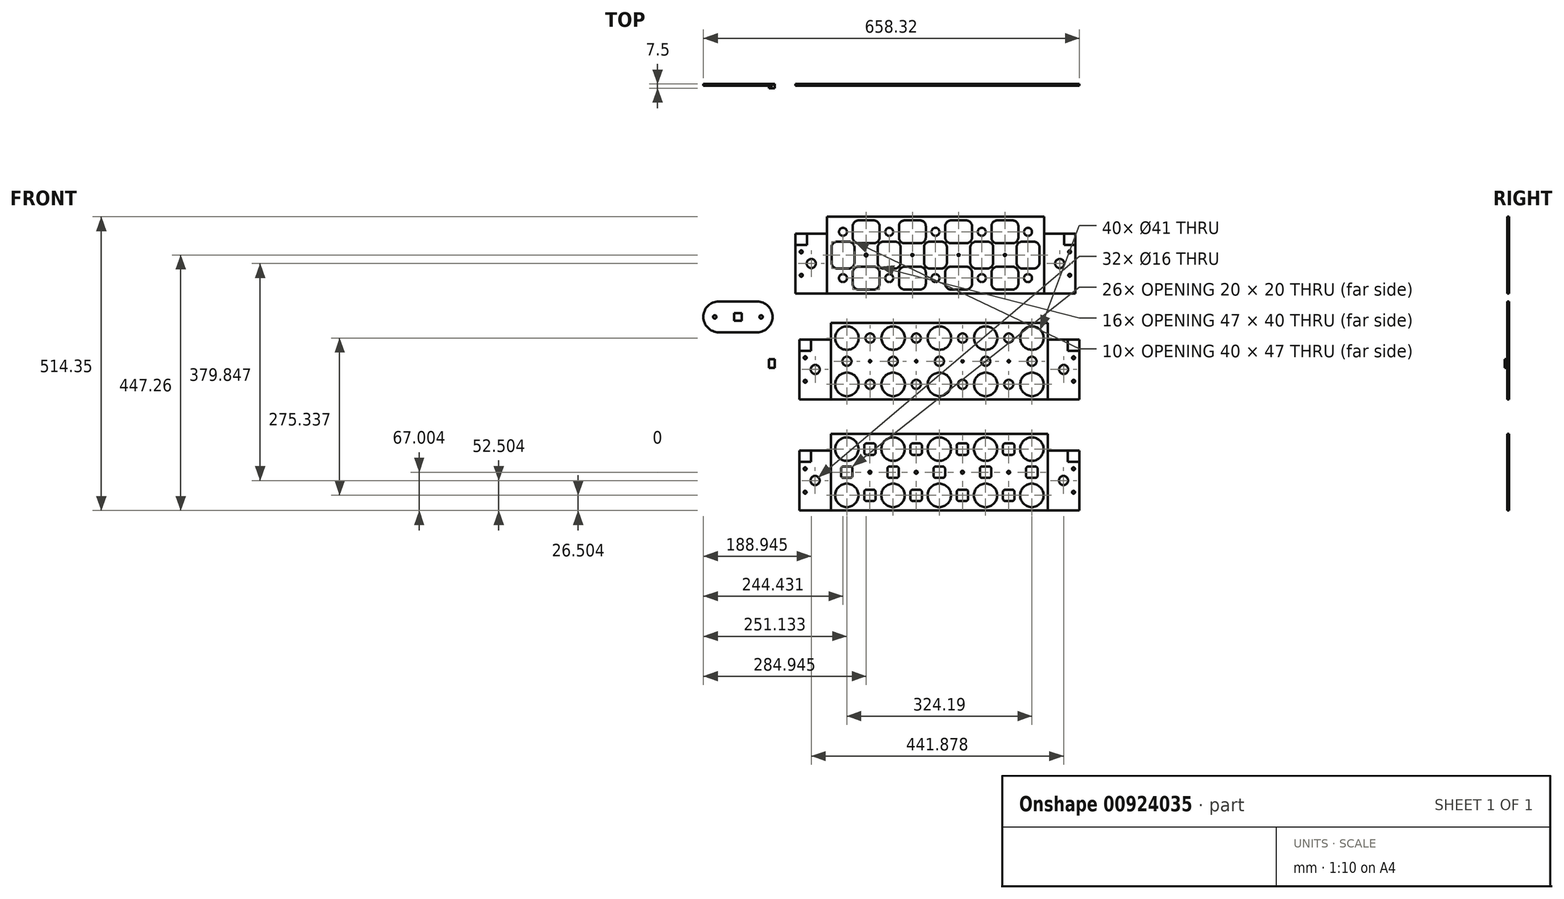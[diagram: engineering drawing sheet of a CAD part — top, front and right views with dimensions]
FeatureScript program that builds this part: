
annotation { "Feature Type Name" : "Feature", "Feature Type Description" : "" }
export const myFeature = defineFeature(function(context is Context, id is Id, definition is map)
    precondition{}
    {
        {
            var Q0;
            Q0=qCreatedBy(makeId("Front.planeOp"),FACE);
            var sketch = newSketch(context, id + "F0", { "sketchPlane" : qUnion([Q0])});
            skLineSegment(sketch, "E0.bottom", {"start": v(-471.38, 281.14) * mm, "end": v(-91.38, 281.14) * mm});
            skLineSegment(sketch, "E0.top", {"start": v(-471.38, 146.64) * mm, "end": v(-91.38, 146.64) * mm});
            skLineSegment(sketch, "E0.left", {"start": v(-471.38, 281.14) * mm, "end": v(-471.38, 146.64) * mm});
            skLineSegment(sketch, "E0.right", {"start": v(-91.38, 281.14) * mm, "end": v(-91.38, 146.64) * mm});
            skLineSegment(sketch, "E1.bottom", {"start": v(-471.38, 251.64) * mm, "end": v(-526.38, 251.64) * mm});
            skLineSegment(sketch, "E1.top", {"start": v(-471.38, 146.64) * mm, "end": v(-526.38, 146.64) * mm});
            skLineSegment(sketch, "E1.left", {"start": v(-471.38, 251.64) * mm, "end": v(-471.38, 146.64) * mm});
            skLineSegment(sketch, "E1.right", {"start": v(-526.38, 251.64) * mm, "end": v(-526.38, 146.64) * mm});
            skLineSegment(sketch, "E2.bottom", {"start": v(-91.38, 251.64) * mm, "end": v(-36.38, 251.64) * mm});
            skLineSegment(sketch, "E2.top", {"start": v(-91.38, 146.64) * mm, "end": v(-36.38, 146.64) * mm});
            skLineSegment(sketch, "E2.left", {"start": v(-91.38, 251.64) * mm, "end": v(-91.38, 146.64) * mm});
            skLineSegment(sketch, "E2.right", {"start": v(-36.38, 251.64) * mm, "end": v(-36.38, 146.64) * mm});
            skCircle(sketch, "E3", {"center": v(-443.38, 173.64) * mm, "radius": 7 * mm});
            skCircle(sketch, "E4.0.1.0", {"center": v(-443.38, 254.64) * mm, "radius": 7 * mm});
            skCircle(sketch, "E4.1.0.0", {"center": v(-362.38, 173.64) * mm, "radius": 7 * mm});
            skCircle(sketch, "E4.1.1.0", {"center": v(-362.38, 254.64) * mm, "radius": 7 * mm});
            skCircle(sketch, "E4.2.0.0", {"center": v(-281.38, 173.64) * mm, "radius": 7 * mm});
            skCircle(sketch, "E4.2.1.0", {"center": v(-281.38, 254.64) * mm, "radius": 7 * mm});
            skCircle(sketch, "E4.3.0.0", {"center": v(-200.38, 173.64) * mm, "radius": 7 * mm});
            skCircle(sketch, "E4.3.1.0", {"center": v(-200.38, 254.64) * mm, "radius": 7 * mm});
            skCircle(sketch, "E4.4.0.0", {"center": v(-119.38, 173.64) * mm, "radius": 7 * mm});
            skCircle(sketch, "E4.4.1.0", {"center": v(-119.38, 254.64) * mm, "radius": 7 * mm});
            skLineSegment(sketch, "E4.direction1", {"start": v(-443.38, 173.64) * mm, "end": v(-362.38, 173.64) * mm, "construction": true});
            skLineSegment(sketch, "E4.direction2", {"start": v(-443.38, 173.64) * mm, "end": v(-443.38, 254.64) * mm, "construction": true});
            skCircle(sketch, "E5", {"center": v(-498.88, 199.14) * mm, "radius": 8 * mm});
            skCircle(sketch, "E6", {"center": v(-63.88, 199.14) * mm, "radius": 8 * mm});
            skPoint(sketch, "E7", {"position": v(-63.88, 251.64) * mm});
            skPoint(sketch, "E8", {"position": v(-498.88, 251.64) * mm});
            skLineSegment(sketch, "E9.bottom", {"start": v(-526.38, 166.64) * mm, "end": v(-506.38, 166.64) * mm});
            skLineSegment(sketch, "E9.top", {"start": v(-526.38, 146.64) * mm, "end": v(-506.38, 146.64) * mm});
            skLineSegment(sketch, "E9.left", {"start": v(-526.38, 166.64) * mm, "end": v(-526.38, 146.64) * mm});
            skLineSegment(sketch, "E9.right", {"start": v(-506.38, 166.64) * mm, "end": v(-506.38, 146.64) * mm});
            skLineSegment(sketch, "E10.bottom", {"start": v(-526.38, 251.64) * mm, "end": v(-506.38, 251.64) * mm});
            skLineSegment(sketch, "E10.top", {"start": v(-526.38, 231.64) * mm, "end": v(-506.38, 231.64) * mm});
            skLineSegment(sketch, "E10.left", {"start": v(-526.38, 251.64) * mm, "end": v(-526.38, 231.64) * mm});
            skLineSegment(sketch, "E10.right", {"start": v(-506.38, 251.64) * mm, "end": v(-506.38, 231.64) * mm});
            skLineSegment(sketch, "E11.bottom", {"start": v(-36.38, 251.64) * mm, "end": v(-56.38, 251.64) * mm});
            skLineSegment(sketch, "E11.top", {"start": v(-36.38, 231.64) * mm, "end": v(-56.38, 231.64) * mm});
            skLineSegment(sketch, "E11.left", {"start": v(-36.38, 251.64) * mm, "end": v(-36.38, 231.64) * mm});
            skLineSegment(sketch, "E11.right", {"start": v(-56.38, 251.64) * mm, "end": v(-56.38, 231.64) * mm});
            skLineSegment(sketch, "E12.bottom", {"start": v(-36.38, 146.64) * mm, "end": v(-56.38, 146.64) * mm});
            skLineSegment(sketch, "E12.top", {"start": v(-36.38, 166.64) * mm, "end": v(-56.38, 166.64) * mm});
            skLineSegment(sketch, "E12.left", {"start": v(-36.38, 146.64) * mm, "end": v(-36.38, 166.64) * mm});
            skLineSegment(sketch, "E12.right", {"start": v(-56.38, 146.64) * mm, "end": v(-56.38, 166.64) * mm});
            skPoint(sketch, "E13", {"position": v(-506.38, 241.64) * mm});
            skPoint(sketch, "E14", {"position": v(-506.38, 156.64) * mm});
            skPoint(sketch, "E15", {"position": v(-56.38, 241.64) * mm});
            skPoint(sketch, "E16", {"position": v(-56.38, 156.64) * mm});
            skCircle(sketch, "E17", {"center": v(-402.88, 214.14) * mm, "radius": 2.55 * mm});
            skCircle(sketch, "E18.1.0.0", {"center": v(-321.88, 214.14) * mm, "radius": 2 * mm});
            skCircle(sketch, "E18.2.0.0", {"center": v(-240.88, 214.14) * mm, "radius": 2 * mm});
            skCircle(sketch, "E18.3.0.0", {"center": v(-159.88, 214.14) * mm, "radius": 2 * mm});
            skPoint(sketch, "E19", {"position": v(-36.38, 199.14) * mm});
            skPoint(sketch, "E20", {"position": v(-516.38, 231.64) * mm});
            skPoint(sketch, "E21", {"position": v(-516.38, 166.64) * mm});
            skPoint(sketch, "E22", {"position": v(-46.38, 231.64) * mm});
            skPoint(sketch, "E23", {"position": v(-46.38, 166.64) * mm});
            skCircle(sketch, "E24", {"center": v(-516.38, 219.64) * mm, "radius": 2.55 * mm});
            skCircle(sketch, "E25", {"center": v(-516.38, 178.64) * mm, "radius": 2.55 * mm});
            skCircle(sketch, "E26", {"center": v(-46.38, 219.64) * mm, "radius": 2.55 * mm});
            skCircle(sketch, "E27", {"center": v(-46.38, 178.64) * mm, "radius": 2.55 * mm});
            skLineSegment(sketch, "E28.bottom", {"start": v(-464.5, 95.13) * mm, "end": v(-84.5, 95.13) * mm});
            skLineSegment(sketch, "E28.top", {"start": v(-464.5, -38.87) * mm, "end": v(-84.5, -38.87) * mm});
            skLineSegment(sketch, "E28.left", {"start": v(-464.5, 95.13) * mm, "end": v(-464.5, -38.87) * mm});
            skLineSegment(sketch, "E28.right", {"start": v(-84.5, 95.13) * mm, "end": v(-84.5, -38.87) * mm});
            skLineSegment(sketch, "E29.bottom", {"start": v(-464.5, 66.13) * mm, "end": v(-519.5, 66.13) * mm});
            skLineSegment(sketch, "E29.top", {"start": v(-464.5, -38.87) * mm, "end": v(-519.5, -38.87) * mm});
            skLineSegment(sketch, "E29.left", {"start": v(-464.5, 66.13) * mm, "end": v(-464.5, -38.87) * mm});
            skLineSegment(sketch, "E29.right", {"start": v(-519.5, 66.13) * mm, "end": v(-519.5, -38.87) * mm});
            skLineSegment(sketch, "E30.bottom", {"start": v(-84.5, 66.13) * mm, "end": v(-29.5, 66.13) * mm});
            skLineSegment(sketch, "E30.top", {"start": v(-84.5, -38.87) * mm, "end": v(-29.5, -38.87) * mm});
            skLineSegment(sketch, "E30.left", {"start": v(-84.5, 66.13) * mm, "end": v(-84.5, -38.87) * mm});
            skLineSegment(sketch, "E30.right", {"start": v(-29.5, 66.13) * mm, "end": v(-29.5, -38.87) * mm});
            skCircle(sketch, "E31", {"center": v(-436.5, -12.37) * mm, "radius": 20.5 * mm});
            skCircle(sketch, "E32.0.1.0", {"center": v(-436.5, 68.63) * mm, "radius": 20.5 * mm});
            skCircle(sketch, "E32.1.0.0", {"center": v(-355.5, -12.37) * mm, "radius": 20.5 * mm});
            skCircle(sketch, "E32.1.1.0", {"center": v(-355.5, 68.63) * mm, "radius": 20.5 * mm});
            skCircle(sketch, "E32.2.0.0", {"center": v(-274.5, -12.37) * mm, "radius": 20.5 * mm});
            skCircle(sketch, "E32.2.1.0", {"center": v(-274.5, 68.63) * mm, "radius": 20.5 * mm});
            skCircle(sketch, "E32.3.0.0", {"center": v(-193.5, -12.37) * mm, "radius": 20.5 * mm});
            skCircle(sketch, "E32.3.1.0", {"center": v(-193.5, 68.63) * mm, "radius": 20.5 * mm});
            skCircle(sketch, "E32.4.0.0", {"center": v(-112.5, -12.37) * mm, "radius": 20.5 * mm});
            skCircle(sketch, "E32.4.1.0", {"center": v(-112.5, 68.63) * mm, "radius": 20.5 * mm});
            skLineSegment(sketch, "E32.direction1", {"start": v(-436.5, -12.37) * mm, "end": v(-355.5, -12.37) * mm});
            skLineSegment(sketch, "E32.direction2", {"start": v(-436.5, -12.37) * mm, "end": v(-436.5, 68.63) * mm, "construction": true});
            skCircle(sketch, "E33", {"center": v(-396, -12.37) * mm, "radius": 8 * mm});
            skPoint(sketch, "E33.centerSnap0", {"position": v(-396, -12.37) * mm});
            skCircle(sketch, "E34.0.1.0", {"center": v(-396, 68.63) * mm, "radius": 8 * mm});
            skCircle(sketch, "E34.1.0.0", {"center": v(-315, -12.37) * mm, "radius": 8 * mm});
            skCircle(sketch, "E34.1.1.0", {"center": v(-315, 68.63) * mm, "radius": 8 * mm});
            skCircle(sketch, "E34.2.0.0", {"center": v(-234, -12.37) * mm, "radius": 8 * mm});
            skCircle(sketch, "E34.2.1.0", {"center": v(-234, 68.63) * mm, "radius": 8 * mm});
            skCircle(sketch, "E34.3.0.0", {"center": v(-153, -12.37) * mm, "radius": 8 * mm});
            skCircle(sketch, "E34.3.1.0", {"center": v(-153, 68.63) * mm, "radius": 8 * mm});
            skLineSegment(sketch, "E34.direction1", {"start": v(-396, -12.37) * mm, "end": v(-315, -12.37) * mm, "construction": true});
            skLineSegment(sketch, "E34.direction2", {"start": v(-396, -12.37) * mm, "end": v(-396, 68.63) * mm, "construction": true});
            skCircle(sketch, "E35", {"center": v(-436.5, 28.13) * mm, "radius": 8 * mm});
            skCircle(sketch, "E36.1.0.0", {"center": v(-355.5, 28.13) * mm, "radius": 8 * mm});
            skCircle(sketch, "E36.2.0.0", {"center": v(-274.5, 28.13) * mm, "radius": 8 * mm});
            skCircle(sketch, "E36.3.0.0", {"center": v(-193.5, 28.13) * mm, "radius": 8 * mm});
            skCircle(sketch, "E36.4.0.0", {"center": v(-112.5, 28.13) * mm, "radius": 8 * mm});
            skLineSegment(sketch, "E36.direction1", {"start": v(-436.5, 28.13) * mm, "end": v(-355.5, 28.13) * mm, "construction": true});
            skCircle(sketch, "E37", {"center": v(-492, 13.63) * mm, "radius": 8 * mm});
            skCircle(sketch, "E38", {"center": v(-57, 13.63) * mm, "radius": 8 * mm});
            skPoint(sketch, "E39", {"position": v(-57, 66.13) * mm});
            skPoint(sketch, "E40", {"position": v(-492, 66.13) * mm});
            skLineSegment(sketch, "E41.bottom", {"start": v(-519.5, -18.87) * mm, "end": v(-499.5, -18.87) * mm});
            skLineSegment(sketch, "E41.top", {"start": v(-519.5, -38.87) * mm, "end": v(-499.5, -38.87) * mm});
            skLineSegment(sketch, "E41.left", {"start": v(-519.5, -18.87) * mm, "end": v(-519.5, -38.87) * mm});
            skLineSegment(sketch, "E41.right", {"start": v(-499.5, -18.87) * mm, "end": v(-499.5, -38.87) * mm});
            skLineSegment(sketch, "E42.bottom", {"start": v(-519.5, 66.13) * mm, "end": v(-499.5, 66.13) * mm});
            skLineSegment(sketch, "E42.top", {"start": v(-519.5, 46.13) * mm, "end": v(-499.5, 46.13) * mm});
            skLineSegment(sketch, "E42.left", {"start": v(-519.5, 66.13) * mm, "end": v(-519.5, 46.13) * mm});
            skLineSegment(sketch, "E42.right", {"start": v(-499.5, 66.13) * mm, "end": v(-499.5, 46.13) * mm});
            skLineSegment(sketch, "E43.bottom", {"start": v(-29.5, 66.13) * mm, "end": v(-49.5, 66.13) * mm});
            skLineSegment(sketch, "E43.top", {"start": v(-29.5, 46.13) * mm, "end": v(-49.5, 46.13) * mm});
            skLineSegment(sketch, "E43.left", {"start": v(-29.5, 66.13) * mm, "end": v(-29.5, 46.13) * mm});
            skLineSegment(sketch, "E43.right", {"start": v(-49.5, 66.13) * mm, "end": v(-49.5, 46.13) * mm});
            skLineSegment(sketch, "E44.bottom", {"start": v(-29.5, -38.87) * mm, "end": v(-49.5, -38.87) * mm});
            skLineSegment(sketch, "E44.top", {"start": v(-29.5, -18.87) * mm, "end": v(-49.5, -18.87) * mm});
            skLineSegment(sketch, "E44.left", {"start": v(-29.5, -38.87) * mm, "end": v(-29.5, -18.87) * mm});
            skLineSegment(sketch, "E44.right", {"start": v(-49.5, -38.87) * mm, "end": v(-49.5, -18.87) * mm});
            skPoint(sketch, "E45", {"position": v(-499.5, 56.13) * mm});
            skPoint(sketch, "E46", {"position": v(-499.5, -28.87) * mm});
            skPoint(sketch, "E47", {"position": v(-49.5, 56.13) * mm});
            skPoint(sketch, "E48", {"position": v(-49.5, -28.87) * mm});
            skCircle(sketch, "E49", {"center": v(-396, 28.13) * mm, "radius": 2 * mm});
            skCircle(sketch, "E50.1.0.0", {"center": v(-315, 28.13) * mm, "radius": 2 * mm});
            skCircle(sketch, "E50.2.0.0", {"center": v(-234, 28.13) * mm, "radius": 2 * mm});
            skCircle(sketch, "E50.3.0.0", {"center": v(-153, 28.13) * mm, "radius": 2 * mm});
            skLineSegment(sketch, "E50.direction1", {"start": v(-396, 28.13) * mm, "end": v(-315, 28.13) * mm, "construction": true});
            skPoint(sketch, "E51", {"position": v(-29.5, 13.63) * mm});
            skPoint(sketch, "E52", {"position": v(-509.5, 46.13) * mm});
            skPoint(sketch, "E53", {"position": v(-509.5, -18.87) * mm});
            skPoint(sketch, "E54", {"position": v(-39.5, 46.13) * mm});
            skPoint(sketch, "E55", {"position": v(-39.5, -18.87) * mm});
            skCircle(sketch, "E56", {"center": v(-509.5, 34.13) * mm, "radius": 2.55 * mm});
            skCircle(sketch, "E57", {"center": v(-509.5, -6.87) * mm, "radius": 2.55 * mm});
            skCircle(sketch, "E58", {"center": v(-39.5, 34.13) * mm, "radius": 2.55 * mm});
            skCircle(sketch, "E59", {"center": v(-39.5, -6.87) * mm, "radius": 2.55 * mm});
            skLineSegment(sketch, "E60.bottom", {"start": v(-389.38, 153.64) * mm, "end": v(-416.38, 153.64) * mm});
            skLineSegment(sketch, "E60.top", {"start": v(-389.38, 193.64) * mm, "end": v(-416.38, 193.64) * mm});
            skLineSegment(sketch, "E60.left", {"start": v(-379.38, 163.64) * mm, "end": v(-379.38, 183.64) * mm});
            skLineSegment(sketch, "E60.right", {"start": v(-426.38, 163.64) * mm, "end": v(-426.38, 183.64) * mm});
            skPoint(sketch, "E60.middle", {"position": v(-402.88, 173.64) * mm});
            skPoint(sketch, "E61.visualSharp", {"position": v(-426.38, 193.64) * mm});
            skArc(sketch, "E61.filletArc", {"start": v(-416.38, 193.64) * mm, "mid": v(-423.46, 190.71) * mm, "end": v(-426.38, 183.64) * mm});
            skPoint(sketch, "E62.visualSharp", {"position": v(-426.38, 153.64) * mm});
            skArc(sketch, "E62.filletArc", {"start": v(-426.38, 163.64) * mm, "mid": v(-423.46, 156.57) * mm, "end": v(-416.38, 153.64) * mm});
            skPoint(sketch, "E63.visualSharp", {"position": v(-379.38, 193.64) * mm});
            skArc(sketch, "E63.filletArc", {"start": v(-379.38, 183.64) * mm, "mid": v(-382.31, 190.71) * mm, "end": v(-389.38, 193.64) * mm});
            skPoint(sketch, "E64.visualSharp", {"position": v(-379.38, 153.64) * mm});
            skArc(sketch, "E64.filletArc", {"start": v(-389.38, 153.64) * mm, "mid": v(-382.31, 156.57) * mm, "end": v(-379.38, 163.64) * mm});
            skPoint(sketch, "E65.0.1.0", {"position": v(-379.38, 274.64) * mm});
            skArc(sketch, "E65.0.1.1", {"start": v(-389.38, 234.64) * mm, "mid": v(-382.31, 237.57) * mm, "end": v(-379.38, 244.64) * mm});
            skPoint(sketch, "E65.0.1.2", {"position": v(-426.38, 274.64) * mm});
            skArc(sketch, "E65.0.1.3", {"start": v(-379.38, 264.64) * mm, "mid": v(-382.31, 271.71) * mm, "end": v(-389.38, 274.64) * mm});
            skLineSegment(sketch, "E65.0.1.4", {"start": v(-426.38, 244.64) * mm, "end": v(-426.38, 264.64) * mm});
            skPoint(sketch, "E65.0.1.5", {"position": v(-426.38, 234.64) * mm});
            skLineSegment(sketch, "E65.0.1.6", {"start": v(-389.38, 274.64) * mm, "end": v(-416.38, 274.64) * mm});
            skArc(sketch, "E65.0.1.7", {"start": v(-426.38, 244.64) * mm, "mid": v(-423.46, 237.57) * mm, "end": v(-416.38, 234.64) * mm});
            skLineSegment(sketch, "E65.0.1.8", {"start": v(-379.38, 244.64) * mm, "end": v(-379.38, 264.64) * mm});
            skLineSegment(sketch, "E65.0.1.9", {"start": v(-389.38, 234.64) * mm, "end": v(-416.38, 234.64) * mm});
            skPoint(sketch, "E65.0.1.10", {"position": v(-379.38, 234.64) * mm});
            skPoint(sketch, "E65.0.1.11", {"position": v(-402.88, 254.64) * mm});
            skArc(sketch, "E65.0.1.12", {"start": v(-416.38, 274.64) * mm, "mid": v(-423.46, 271.71) * mm, "end": v(-426.38, 264.64) * mm});
            skPoint(sketch, "E65.1.0.0", {"position": v(-298.38, 193.64) * mm});
            skArc(sketch, "E65.1.0.1", {"start": v(-308.38, 153.64) * mm, "mid": v(-301.31, 156.57) * mm, "end": v(-298.38, 163.64) * mm});
            skPoint(sketch, "E65.1.0.2", {"position": v(-345.38, 193.64) * mm});
            skArc(sketch, "E65.1.0.3", {"start": v(-298.38, 183.64) * mm, "mid": v(-301.31, 190.71) * mm, "end": v(-308.38, 193.64) * mm});
            skLineSegment(sketch, "E65.1.0.4", {"start": v(-345.38, 163.64) * mm, "end": v(-345.38, 183.64) * mm});
            skPoint(sketch, "E65.1.0.5", {"position": v(-345.38, 153.64) * mm});
            skLineSegment(sketch, "E65.1.0.6", {"start": v(-308.38, 193.64) * mm, "end": v(-335.38, 193.64) * mm});
            skArc(sketch, "E65.1.0.7", {"start": v(-345.38, 163.64) * mm, "mid": v(-342.46, 156.57) * mm, "end": v(-335.38, 153.64) * mm});
            skLineSegment(sketch, "E65.1.0.8", {"start": v(-298.38, 163.64) * mm, "end": v(-298.38, 183.64) * mm});
            skLineSegment(sketch, "E65.1.0.9", {"start": v(-308.38, 153.64) * mm, "end": v(-335.38, 153.64) * mm});
            skPoint(sketch, "E65.1.0.10", {"position": v(-298.38, 153.64) * mm});
            skPoint(sketch, "E65.1.0.11", {"position": v(-321.88, 173.64) * mm});
            skArc(sketch, "E65.1.0.12", {"start": v(-335.38, 193.64) * mm, "mid": v(-342.46, 190.71) * mm, "end": v(-345.38, 183.64) * mm});
            skPoint(sketch, "E65.1.1.0", {"position": v(-298.38, 274.64) * mm});
            skArc(sketch, "E65.1.1.1", {"start": v(-308.38, 234.64) * mm, "mid": v(-301.31, 237.57) * mm, "end": v(-298.38, 244.64) * mm});
            skPoint(sketch, "E65.1.1.2", {"position": v(-345.38, 274.64) * mm});
            skArc(sketch, "E65.1.1.3", {"start": v(-298.38, 264.64) * mm, "mid": v(-301.31, 271.71) * mm, "end": v(-308.38, 274.64) * mm});
            skLineSegment(sketch, "E65.1.1.4", {"start": v(-345.38, 244.64) * mm, "end": v(-345.38, 264.64) * mm});
            skPoint(sketch, "E65.1.1.5", {"position": v(-345.38, 234.64) * mm});
            skLineSegment(sketch, "E65.1.1.6", {"start": v(-308.38, 274.64) * mm, "end": v(-335.38, 274.64) * mm});
            skArc(sketch, "E65.1.1.7", {"start": v(-345.38, 244.64) * mm, "mid": v(-342.46, 237.57) * mm, "end": v(-335.38, 234.64) * mm});
            skLineSegment(sketch, "E65.1.1.8", {"start": v(-298.38, 244.64) * mm, "end": v(-298.38, 264.64) * mm});
            skLineSegment(sketch, "E65.1.1.9", {"start": v(-308.38, 234.64) * mm, "end": v(-335.38, 234.64) * mm});
            skPoint(sketch, "E65.1.1.10", {"position": v(-298.38, 234.64) * mm});
            skPoint(sketch, "E65.1.1.11", {"position": v(-321.88, 254.64) * mm});
            skArc(sketch, "E65.1.1.12", {"start": v(-335.38, 274.64) * mm, "mid": v(-342.46, 271.71) * mm, "end": v(-345.38, 264.64) * mm});
            skPoint(sketch, "E65.2.0.0", {"position": v(-217.38, 193.64) * mm});
            skArc(sketch, "E65.2.0.1", {"start": v(-227.38, 153.64) * mm, "mid": v(-220.31, 156.57) * mm, "end": v(-217.38, 163.64) * mm});
            skPoint(sketch, "E65.2.0.2", {"position": v(-264.38, 193.64) * mm});
            skArc(sketch, "E65.2.0.3", {"start": v(-217.38, 183.64) * mm, "mid": v(-220.31, 190.71) * mm, "end": v(-227.38, 193.64) * mm});
            skLineSegment(sketch, "E65.2.0.4", {"start": v(-264.38, 163.64) * mm, "end": v(-264.38, 183.64) * mm});
            skPoint(sketch, "E65.2.0.5", {"position": v(-264.38, 153.64) * mm});
            skLineSegment(sketch, "E65.2.0.6", {"start": v(-227.38, 193.64) * mm, "end": v(-254.38, 193.64) * mm});
            skArc(sketch, "E65.2.0.7", {"start": v(-264.38, 163.64) * mm, "mid": v(-261.46, 156.57) * mm, "end": v(-254.38, 153.64) * mm});
            skLineSegment(sketch, "E65.2.0.8", {"start": v(-217.38, 163.64) * mm, "end": v(-217.38, 183.64) * mm});
            skLineSegment(sketch, "E65.2.0.9", {"start": v(-227.38, 153.64) * mm, "end": v(-254.38, 153.64) * mm});
            skPoint(sketch, "E65.2.0.10", {"position": v(-217.38, 153.64) * mm});
            skPoint(sketch, "E65.2.0.11", {"position": v(-240.88, 173.64) * mm});
            skArc(sketch, "E65.2.0.12", {"start": v(-254.38, 193.64) * mm, "mid": v(-261.46, 190.71) * mm, "end": v(-264.38, 183.64) * mm});
            skPoint(sketch, "E65.2.1.0", {"position": v(-217.38, 274.64) * mm});
            skArc(sketch, "E65.2.1.1", {"start": v(-227.38, 234.64) * mm, "mid": v(-220.31, 237.57) * mm, "end": v(-217.38, 244.64) * mm});
            skPoint(sketch, "E65.2.1.2", {"position": v(-264.38, 274.64) * mm});
            skArc(sketch, "E65.2.1.3", {"start": v(-217.38, 264.64) * mm, "mid": v(-220.31, 271.71) * mm, "end": v(-227.38, 274.64) * mm});
            skLineSegment(sketch, "E65.2.1.4", {"start": v(-264.38, 244.64) * mm, "end": v(-264.38, 264.64) * mm});
            skPoint(sketch, "E65.2.1.5", {"position": v(-264.38, 234.64) * mm});
            skLineSegment(sketch, "E65.2.1.6", {"start": v(-227.38, 274.64) * mm, "end": v(-254.38, 274.64) * mm});
            skArc(sketch, "E65.2.1.7", {"start": v(-264.38, 244.64) * mm, "mid": v(-261.46, 237.57) * mm, "end": v(-254.38, 234.64) * mm});
            skLineSegment(sketch, "E65.2.1.8", {"start": v(-217.38, 244.64) * mm, "end": v(-217.38, 264.64) * mm});
            skLineSegment(sketch, "E65.2.1.9", {"start": v(-227.38, 234.64) * mm, "end": v(-254.38, 234.64) * mm});
            skPoint(sketch, "E65.2.1.10", {"position": v(-217.38, 234.64) * mm});
            skPoint(sketch, "E65.2.1.11", {"position": v(-240.88, 254.64) * mm});
            skArc(sketch, "E65.2.1.12", {"start": v(-254.38, 274.64) * mm, "mid": v(-261.46, 271.71) * mm, "end": v(-264.38, 264.64) * mm});
            skPoint(sketch, "E65.3.0.0", {"position": v(-136.38, 193.64) * mm});
            skArc(sketch, "E65.3.0.1", {"start": v(-146.38, 153.64) * mm, "mid": v(-139.31, 156.57) * mm, "end": v(-136.38, 163.64) * mm});
            skPoint(sketch, "E65.3.0.2", {"position": v(-183.38, 193.64) * mm});
            skArc(sketch, "E65.3.0.3", {"start": v(-136.38, 183.64) * mm, "mid": v(-139.31, 190.71) * mm, "end": v(-146.38, 193.64) * mm});
            skLineSegment(sketch, "E65.3.0.4", {"start": v(-183.38, 163.64) * mm, "end": v(-183.38, 183.64) * mm});
            skPoint(sketch, "E65.3.0.5", {"position": v(-183.38, 153.64) * mm});
            skLineSegment(sketch, "E65.3.0.6", {"start": v(-146.38, 193.64) * mm, "end": v(-173.38, 193.64) * mm});
            skArc(sketch, "E65.3.0.7", {"start": v(-183.38, 163.64) * mm, "mid": v(-180.46, 156.57) * mm, "end": v(-173.38, 153.64) * mm});
            skLineSegment(sketch, "E65.3.0.8", {"start": v(-136.38, 163.64) * mm, "end": v(-136.38, 183.64) * mm});
            skLineSegment(sketch, "E65.3.0.9", {"start": v(-146.38, 153.64) * mm, "end": v(-173.38, 153.64) * mm});
            skPoint(sketch, "E65.3.0.10", {"position": v(-136.38, 153.64) * mm});
            skPoint(sketch, "E65.3.0.11", {"position": v(-159.88, 173.64) * mm});
            skArc(sketch, "E65.3.0.12", {"start": v(-173.38, 193.64) * mm, "mid": v(-180.46, 190.71) * mm, "end": v(-183.38, 183.64) * mm});
            skPoint(sketch, "E65.3.1.0", {"position": v(-136.38, 274.64) * mm});
            skArc(sketch, "E65.3.1.1", {"start": v(-146.38, 234.64) * mm, "mid": v(-139.31, 237.57) * mm, "end": v(-136.38, 244.64) * mm});
            skPoint(sketch, "E65.3.1.2", {"position": v(-183.38, 274.64) * mm});
            skArc(sketch, "E65.3.1.3", {"start": v(-136.38, 264.64) * mm, "mid": v(-139.31, 271.71) * mm, "end": v(-146.38, 274.64) * mm});
            skLineSegment(sketch, "E65.3.1.4", {"start": v(-183.38, 244.64) * mm, "end": v(-183.38, 264.64) * mm});
            skPoint(sketch, "E65.3.1.5", {"position": v(-183.38, 234.64) * mm});
            skLineSegment(sketch, "E65.3.1.6", {"start": v(-146.38, 274.64) * mm, "end": v(-173.38, 274.64) * mm});
            skArc(sketch, "E65.3.1.7", {"start": v(-183.38, 244.64) * mm, "mid": v(-180.46, 237.57) * mm, "end": v(-173.38, 234.64) * mm});
            skLineSegment(sketch, "E65.3.1.8", {"start": v(-136.38, 244.64) * mm, "end": v(-136.38, 264.64) * mm});
            skLineSegment(sketch, "E65.3.1.9", {"start": v(-146.38, 234.64) * mm, "end": v(-173.38, 234.64) * mm});
            skPoint(sketch, "E65.3.1.10", {"position": v(-136.38, 234.64) * mm});
            skPoint(sketch, "E65.3.1.11", {"position": v(-159.88, 254.64) * mm});
            skArc(sketch, "E65.3.1.12", {"start": v(-173.38, 274.64) * mm, "mid": v(-180.46, 271.71) * mm, "end": v(-183.38, 264.64) * mm});
            skLineSegment(sketch, "E65.direction1", {"start": v(-426.38, 153.64) * mm, "end": v(-345.38, 153.64) * mm, "construction": true});
            skLineSegment(sketch, "E65.direction2", {"start": v(-426.38, 153.64) * mm, "end": v(-426.38, 234.64) * mm, "construction": true});
            skLineSegment(sketch, "E66.bottom", {"start": v(-423.4, 227.55) * mm, "end": v(-423.4, 200.55) * mm});
            skLineSegment(sketch, "E66.top", {"start": v(-463.4, 227.55) * mm, "end": v(-463.4, 200.55) * mm});
            skLineSegment(sketch, "E66.left", {"start": v(-433.4, 237.55) * mm, "end": v(-453.4, 237.55) * mm});
            skLineSegment(sketch, "E66.right", {"start": v(-433.4, 190.55) * mm, "end": v(-453.4, 190.55) * mm});
            skPoint(sketch, "E66.middle", {"position": v(-443.4, 214.05) * mm});
            skPoint(sketch, "E67.visualSharp", {"position": v(-463.4, 190.55) * mm});
            skArc(sketch, "E67.filletArc", {"start": v(-463.4, 200.55) * mm, "mid": v(-460.47, 193.48) * mm, "end": v(-453.4, 190.55) * mm});
            skPoint(sketch, "E68.visualSharp", {"position": v(-423.4, 190.55) * mm});
            skArc(sketch, "E68.filletArc", {"start": v(-433.4, 190.55) * mm, "mid": v(-426.33, 193.48) * mm, "end": v(-423.4, 200.55) * mm});
            skPoint(sketch, "E69.visualSharp", {"position": v(-463.4, 237.55) * mm});
            skArc(sketch, "E69.filletArc", {"start": v(-453.4, 237.55) * mm, "mid": v(-460.47, 234.62) * mm, "end": v(-463.4, 227.55) * mm});
            skPoint(sketch, "E70.visualSharp", {"position": v(-423.4, 237.55) * mm});
            skArc(sketch, "E70.filletArc", {"start": v(-423.4, 227.55) * mm, "mid": v(-426.33, 234.62) * mm, "end": v(-433.4, 237.55) * mm});
            skPoint(sketch, "E71", {"position": v(-443.38, 214.14) * mm});
            skLineSegment(sketch, "E72.1.0.0", {"start": v(-342.4, 227.55) * mm, "end": v(-342.4, 200.55) * mm});
            skPoint(sketch, "E72.1.0.1", {"position": v(-382.4, 190.55) * mm});
            skLineSegment(sketch, "E72.1.0.2", {"start": v(-352.4, 190.55) * mm, "end": v(-372.4, 190.55) * mm});
            skPoint(sketch, "E72.1.0.3", {"position": v(-342.4, 237.55) * mm});
            skLineSegment(sketch, "E72.1.0.4", {"start": v(-352.4, 237.55) * mm, "end": v(-372.4, 237.55) * mm});
            skLineSegment(sketch, "E72.1.0.5", {"start": v(-382.4, 227.55) * mm, "end": v(-382.4, 200.55) * mm});
            skPoint(sketch, "E72.1.0.6", {"position": v(-382.4, 237.55) * mm});
            skPoint(sketch, "E72.1.0.7", {"position": v(-362.4, 214.05) * mm});
            skPoint(sketch, "E72.1.0.8", {"position": v(-342.4, 190.55) * mm});
            skArc(sketch, "E72.1.0.9", {"start": v(-372.4, 237.55) * mm, "mid": v(-379.47, 234.62) * mm, "end": v(-382.4, 227.55) * mm});
            skArc(sketch, "E72.1.0.10", {"start": v(-342.4, 227.55) * mm, "mid": v(-345.33, 234.62) * mm, "end": v(-352.4, 237.55) * mm});
            skArc(sketch, "E72.1.0.11", {"start": v(-382.4, 200.55) * mm, "mid": v(-379.47, 193.48) * mm, "end": v(-372.4, 190.55) * mm});
            skArc(sketch, "E72.1.0.12", {"start": v(-352.4, 190.55) * mm, "mid": v(-345.33, 193.48) * mm, "end": v(-342.4, 200.55) * mm});
            skLineSegment(sketch, "E72.2.0.0", {"start": v(-261.4, 227.55) * mm, "end": v(-261.4, 200.55) * mm});
            skPoint(sketch, "E72.2.0.1", {"position": v(-301.4, 190.55) * mm});
            skLineSegment(sketch, "E72.2.0.2", {"start": v(-271.4, 190.55) * mm, "end": v(-291.4, 190.55) * mm});
            skPoint(sketch, "E72.2.0.3", {"position": v(-261.4, 237.55) * mm});
            skLineSegment(sketch, "E72.2.0.4", {"start": v(-271.4, 237.55) * mm, "end": v(-291.4, 237.55) * mm});
            skLineSegment(sketch, "E72.2.0.5", {"start": v(-301.4, 227.55) * mm, "end": v(-301.4, 200.55) * mm});
            skPoint(sketch, "E72.2.0.6", {"position": v(-301.4, 237.55) * mm});
            skPoint(sketch, "E72.2.0.7", {"position": v(-281.4, 214.05) * mm});
            skPoint(sketch, "E72.2.0.8", {"position": v(-261.4, 190.55) * mm});
            skArc(sketch, "E72.2.0.9", {"start": v(-291.4, 237.55) * mm, "mid": v(-298.47, 234.62) * mm, "end": v(-301.4, 227.55) * mm});
            skArc(sketch, "E72.2.0.10", {"start": v(-261.4, 227.55) * mm, "mid": v(-264.33, 234.62) * mm, "end": v(-271.4, 237.55) * mm});
            skArc(sketch, "E72.2.0.11", {"start": v(-301.4, 200.55) * mm, "mid": v(-298.47, 193.48) * mm, "end": v(-291.4, 190.55) * mm});
            skArc(sketch, "E72.2.0.12", {"start": v(-271.4, 190.55) * mm, "mid": v(-264.33, 193.48) * mm, "end": v(-261.4, 200.55) * mm});
            skLineSegment(sketch, "E72.3.0.0", {"start": v(-180.4, 227.55) * mm, "end": v(-180.4, 200.55) * mm});
            skPoint(sketch, "E72.3.0.1", {"position": v(-220.4, 190.55) * mm});
            skLineSegment(sketch, "E72.3.0.2", {"start": v(-190.4, 190.55) * mm, "end": v(-210.4, 190.55) * mm});
            skPoint(sketch, "E72.3.0.3", {"position": v(-180.4, 237.55) * mm});
            skLineSegment(sketch, "E72.3.0.4", {"start": v(-190.4, 237.55) * mm, "end": v(-210.4, 237.55) * mm});
            skLineSegment(sketch, "E72.3.0.5", {"start": v(-220.4, 227.55) * mm, "end": v(-220.4, 200.55) * mm});
            skPoint(sketch, "E72.3.0.6", {"position": v(-220.4, 237.55) * mm});
            skPoint(sketch, "E72.3.0.7", {"position": v(-200.4, 214.05) * mm});
            skPoint(sketch, "E72.3.0.8", {"position": v(-180.4, 190.55) * mm});
            skArc(sketch, "E72.3.0.9", {"start": v(-210.4, 237.55) * mm, "mid": v(-217.47, 234.62) * mm, "end": v(-220.4, 227.55) * mm});
            skArc(sketch, "E72.3.0.10", {"start": v(-180.4, 227.55) * mm, "mid": v(-183.33, 234.62) * mm, "end": v(-190.4, 237.55) * mm});
            skArc(sketch, "E72.3.0.11", {"start": v(-220.4, 200.55) * mm, "mid": v(-217.47, 193.48) * mm, "end": v(-210.4, 190.55) * mm});
            skArc(sketch, "E72.3.0.12", {"start": v(-190.4, 190.55) * mm, "mid": v(-183.33, 193.48) * mm, "end": v(-180.4, 200.55) * mm});
            skLineSegment(sketch, "E72.4.0.0", {"start": v(-99.4, 227.55) * mm, "end": v(-99.4, 200.55) * mm});
            skPoint(sketch, "E72.4.0.1", {"position": v(-139.4, 190.55) * mm});
            skLineSegment(sketch, "E72.4.0.2", {"start": v(-109.4, 190.55) * mm, "end": v(-129.4, 190.55) * mm});
            skPoint(sketch, "E72.4.0.3", {"position": v(-99.4, 237.55) * mm});
            skLineSegment(sketch, "E72.4.0.4", {"start": v(-109.4, 237.55) * mm, "end": v(-129.4, 237.55) * mm});
            skLineSegment(sketch, "E72.4.0.5", {"start": v(-139.4, 227.55) * mm, "end": v(-139.4, 200.55) * mm});
            skPoint(sketch, "E72.4.0.6", {"position": v(-139.4, 237.55) * mm});
            skPoint(sketch, "E72.4.0.7", {"position": v(-119.4, 214.05) * mm});
            skPoint(sketch, "E72.4.0.8", {"position": v(-99.4, 190.55) * mm});
            skArc(sketch, "E72.4.0.9", {"start": v(-129.4, 237.55) * mm, "mid": v(-136.47, 234.62) * mm, "end": v(-139.4, 227.55) * mm});
            skArc(sketch, "E72.4.0.10", {"start": v(-99.4, 227.55) * mm, "mid": v(-102.33, 234.62) * mm, "end": v(-109.4, 237.55) * mm});
            skArc(sketch, "E72.4.0.11", {"start": v(-139.4, 200.55) * mm, "mid": v(-136.47, 193.48) * mm, "end": v(-129.4, 190.55) * mm});
            skArc(sketch, "E72.4.0.12", {"start": v(-109.4, 190.55) * mm, "mid": v(-102.33, 193.48) * mm, "end": v(-99.4, 200.55) * mm});
            skLineSegment(sketch, "E72.direction1", {"start": v(-463.4, 190.55) * mm, "end": v(-382.4, 190.55) * mm, "construction": true});
            skLineSegment(sketch, "E73.bottom", {"start": v(-464.7, -99.2) * mm, "end": v(-84.7, -99.2) * mm});
            skLineSegment(sketch, "E73.top", {"start": v(-464.7, -233.2) * mm, "end": v(-84.7, -233.2) * mm});
            skLineSegment(sketch, "E73.left", {"start": v(-464.7, -99.2) * mm, "end": v(-464.7, -233.2) * mm});
            skLineSegment(sketch, "E73.right", {"start": v(-84.7, -99.2) * mm, "end": v(-84.7, -233.2) * mm});
            skLineSegment(sketch, "E74.bottom", {"start": v(-464.7, -128.2) * mm, "end": v(-519.7, -128.2) * mm});
            skLineSegment(sketch, "E74.top", {"start": v(-464.7, -233.2) * mm, "end": v(-519.7, -233.2) * mm});
            skLineSegment(sketch, "E74.left", {"start": v(-464.7, -128.2) * mm, "end": v(-464.7, -233.2) * mm});
            skLineSegment(sketch, "E74.right", {"start": v(-519.7, -128.2) * mm, "end": v(-519.7, -233.2) * mm});
            skLineSegment(sketch, "E75.bottom", {"start": v(-84.7, -128.2) * mm, "end": v(-29.7, -128.2) * mm});
            skLineSegment(sketch, "E75.top", {"start": v(-84.7, -233.2) * mm, "end": v(-29.7, -233.2) * mm});
            skLineSegment(sketch, "E75.left", {"start": v(-84.7, -128.2) * mm, "end": v(-84.7, -233.2) * mm});
            skLineSegment(sketch, "E75.right", {"start": v(-29.7, -128.2) * mm, "end": v(-29.7, -233.2) * mm});
            skCircle(sketch, "E76", {"center": v(-436.7, -206.7) * mm, "radius": 20.5 * mm});
            skCircle(sketch, "E77.0.1.0", {"center": v(-436.7, -125.7) * mm, "radius": 20.5 * mm});
            skCircle(sketch, "E77.1.0.0", {"center": v(-355.7, -206.7) * mm, "radius": 20.5 * mm});
            skCircle(sketch, "E77.1.1.0", {"center": v(-355.7, -125.7) * mm, "radius": 20.5 * mm});
            skCircle(sketch, "E77.2.0.0", {"center": v(-274.7, -206.7) * mm, "radius": 20.5 * mm});
            skCircle(sketch, "E77.2.1.0", {"center": v(-274.7, -125.7) * mm, "radius": 20.5 * mm});
            skCircle(sketch, "E77.3.0.0", {"center": v(-193.7, -206.7) * mm, "radius": 20.5 * mm});
            skCircle(sketch, "E77.3.1.0", {"center": v(-193.7, -125.7) * mm, "radius": 20.5 * mm});
            skCircle(sketch, "E77.4.0.0", {"center": v(-112.7, -206.7) * mm, "radius": 20.5 * mm});
            skCircle(sketch, "E77.4.1.0", {"center": v(-112.7, -125.7) * mm, "radius": 20.5 * mm});
            skLineSegment(sketch, "E77.direction1", {"start": v(-436.7, -206.7) * mm, "end": v(-355.7, -206.7) * mm});
            skLineSegment(sketch, "E77.direction2", {"start": v(-436.7, -206.7) * mm, "end": v(-436.7, -125.7) * mm, "construction": true});
            skPoint(sketch, "E78.centerSnap0", {"position": v(-396.2, -206.7) * mm});
            skCircle(sketch, "E79", {"center": v(-492.2, -180.7) * mm, "radius": 8 * mm});
            skCircle(sketch, "E80", {"center": v(-57.2, -180.7) * mm, "radius": 8 * mm});
            skPoint(sketch, "E81", {"position": v(-57.2, -128.2) * mm});
            skPoint(sketch, "E82", {"position": v(-492.2, -128.2) * mm});
            skLineSegment(sketch, "E83.bottom", {"start": v(-519.7, -213.2) * mm, "end": v(-499.7, -213.2) * mm});
            skLineSegment(sketch, "E83.top", {"start": v(-519.7, -233.2) * mm, "end": v(-499.7, -233.2) * mm});
            skLineSegment(sketch, "E83.left", {"start": v(-519.7, -213.2) * mm, "end": v(-519.7, -233.2) * mm});
            skLineSegment(sketch, "E83.right", {"start": v(-499.7, -213.2) * mm, "end": v(-499.7, -233.2) * mm});
            skLineSegment(sketch, "E84.bottom", {"start": v(-519.7, -128.2) * mm, "end": v(-499.7, -128.2) * mm});
            skLineSegment(sketch, "E84.top", {"start": v(-519.7, -148.2) * mm, "end": v(-499.7, -148.2) * mm});
            skLineSegment(sketch, "E84.left", {"start": v(-519.7, -128.2) * mm, "end": v(-519.7, -148.2) * mm});
            skLineSegment(sketch, "E84.right", {"start": v(-499.7, -128.2) * mm, "end": v(-499.7, -148.2) * mm});
            skLineSegment(sketch, "E85.bottom", {"start": v(-29.7, -128.2) * mm, "end": v(-49.7, -128.2) * mm});
            skLineSegment(sketch, "E85.top", {"start": v(-29.7, -148.2) * mm, "end": v(-49.7, -148.2) * mm});
            skLineSegment(sketch, "E85.left", {"start": v(-29.7, -128.2) * mm, "end": v(-29.7, -148.2) * mm});
            skLineSegment(sketch, "E85.right", {"start": v(-49.7, -128.2) * mm, "end": v(-49.7, -148.2) * mm});
            skLineSegment(sketch, "E86.bottom", {"start": v(-29.7, -233.2) * mm, "end": v(-49.7, -233.2) * mm});
            skLineSegment(sketch, "E86.top", {"start": v(-29.7, -213.2) * mm, "end": v(-49.7, -213.2) * mm});
            skLineSegment(sketch, "E86.left", {"start": v(-29.7, -233.2) * mm, "end": v(-29.7, -213.2) * mm});
            skLineSegment(sketch, "E86.right", {"start": v(-49.7, -233.2) * mm, "end": v(-49.7, -213.2) * mm});
            skPoint(sketch, "E87", {"position": v(-499.7, -138.2) * mm});
            skPoint(sketch, "E88", {"position": v(-499.7, -223.2) * mm});
            skPoint(sketch, "E89", {"position": v(-49.7, -138.2) * mm});
            skPoint(sketch, "E90", {"position": v(-49.7, -223.2) * mm});
            skCircle(sketch, "E91", {"center": v(-396.2, -166.2) * mm, "radius": 2.55 * mm});
            skCircle(sketch, "E92.1.0.0", {"center": v(-315.2, -166.2) * mm, "radius": 2.55 * mm});
            skCircle(sketch, "E92.2.0.0", {"center": v(-234.2, -166.2) * mm, "radius": 2.55 * mm});
            skCircle(sketch, "E92.3.0.0", {"center": v(-153.2, -166.2) * mm, "radius": 2.55 * mm});
            skLineSegment(sketch, "E92.direction1", {"start": v(-396.2, -166.2) * mm, "end": v(-315.2, -166.2) * mm, "construction": true});
            skPoint(sketch, "E93", {"position": v(-29.7, -180.7) * mm});
            skPoint(sketch, "E94", {"position": v(-509.7, -148.2) * mm});
            skPoint(sketch, "E95", {"position": v(-509.7, -213.2) * mm});
            skPoint(sketch, "E96", {"position": v(-39.7, -148.2) * mm});
            skPoint(sketch, "E97", {"position": v(-39.7, -213.2) * mm});
            skCircle(sketch, "E98", {"center": v(-509.7, -160.2) * mm, "radius": 2.55 * mm});
            skCircle(sketch, "E99", {"center": v(-509.7, -201.2) * mm, "radius": 2.55 * mm});
            skCircle(sketch, "E100", {"center": v(-39.7, -160.2) * mm, "radius": 2.55 * mm});
            skCircle(sketch, "E101", {"center": v(-39.7, -201.2) * mm, "radius": 2.55 * mm});
            skPoint(sketch, "E102.middle", {"position": v(-436.7, -166.2) * mm});
            skLineSegment(sketch, "E103.bottom", {"start": v(-390.2, -216.7) * mm, "end": v(-402.2, -216.7) * mm});
            skLineSegment(sketch, "E103.top", {"start": v(-390.2, -196.7) * mm, "end": v(-402.2, -196.7) * mm});
            skLineSegment(sketch, "E103.left", {"start": v(-386.2, -212.7) * mm, "end": v(-386.2, -200.7) * mm});
            skLineSegment(sketch, "E103.right", {"start": v(-406.2, -212.7) * mm, "end": v(-406.2, -200.7) * mm});
            skPoint(sketch, "E104.visualSharp", {"position": v(-406.2, -216.7) * mm});
            skArc(sketch, "E104.filletArc", {"start": v(-406.2, -212.7) * mm, "mid": v(-405.03, -215.53) * mm, "end": v(-402.2, -216.7) * mm});
            skPoint(sketch, "E105.visualSharp", {"position": v(-406.2, -196.7) * mm});
            skArc(sketch, "E105.filletArc", {"start": v(-402.2, -196.7) * mm, "mid": v(-405.03, -197.88) * mm, "end": v(-406.2, -200.7) * mm});
            skPoint(sketch, "E106.visualSharp", {"position": v(-386.2, -196.7) * mm});
            skArc(sketch, "E106.filletArc", {"start": v(-386.2, -200.7) * mm, "mid": v(-387.37, -197.88) * mm, "end": v(-390.2, -196.7) * mm});
            skPoint(sketch, "E107.visualSharp", {"position": v(-386.2, -216.7) * mm});
            skArc(sketch, "E107.filletArc", {"start": v(-390.2, -216.7) * mm, "mid": v(-387.37, -215.53) * mm, "end": v(-386.2, -212.7) * mm});
            skLineSegment(sketch, "E108.bottom", {"start": v(-593.83, 78.82) * mm, "end": v(-660.83, 78.82) * mm});
            skLineSegment(sketch, "E108.top", {"start": v(-593.83, 132.82) * mm, "end": v(-660.83, 132.82) * mm});
            skLineSegment(sketch, "E108.left", {"start": v(-566.83, 105.82) * mm, "end": v(-566.83, 105.82) * mm});
            skLineSegment(sketch, "E108.right", {"start": v(-687.83, 105.82) * mm, "end": v(-687.83, 105.82) * mm});
            skPoint(sketch, "E108.middle", {"position": v(-627.33, 105.82) * mm});
            skPoint(sketch, "E109.visualSharp", {"position": v(-566.83, 132.82) * mm});
            skArc(sketch, "E109.filletArc", {"start": v(-566.83, 105.82) * mm, "mid": v(-574.74, 124.91) * mm, "end": v(-593.83, 132.82) * mm});
            skPoint(sketch, "E110.visualSharp", {"position": v(-566.83, 78.82) * mm});
            skArc(sketch, "E110.filletArc", {"start": v(-593.83, 78.82) * mm, "mid": v(-574.74, 86.73) * mm, "end": v(-566.83, 105.82) * mm});
            skPoint(sketch, "E111.visualSharp", {"position": v(-687.83, 78.82) * mm});
            skArc(sketch, "E111.filletArc", {"start": v(-687.83, 105.82) * mm, "mid": v(-679.92, 86.73) * mm, "end": v(-660.83, 78.82) * mm});
            skPoint(sketch, "E112.visualSharp", {"position": v(-687.83, 132.82) * mm});
            skArc(sketch, "E112.filletArc", {"start": v(-660.83, 132.82) * mm, "mid": v(-679.92, 124.91) * mm, "end": v(-687.83, 105.82) * mm});
            skLineSegment(sketch, "E113.bottom", {"start": v(-620.83, 99.32) * mm, "end": v(-633.83, 99.32) * mm});
            skLineSegment(sketch, "E113.top", {"start": v(-620.83, 112.32) * mm, "end": v(-633.83, 112.32) * mm});
            skLineSegment(sketch, "E113.left", {"start": v(-620.83, 99.32) * mm, "end": v(-620.83, 112.32) * mm});
            skLineSegment(sketch, "E113.right", {"start": v(-633.83, 99.32) * mm, "end": v(-633.83, 112.32) * mm});
            skCircle(sketch, "E114", {"center": v(-667.83, 105.82) * mm, "radius": 3 * mm});
            skCircle(sketch, "E115", {"center": v(-586.83, 105.82) * mm, "radius": 3 * mm});
            skPoint(sketch, "E116.0.1.0", {"position": v(-386.2, -115.7) * mm});
            skLineSegment(sketch, "E116.0.1.1", {"start": v(-390.2, -135.7) * mm, "end": v(-402.2, -135.7) * mm});
            skLineSegment(sketch, "E116.0.1.2", {"start": v(-390.2, -115.7) * mm, "end": v(-402.2, -115.7) * mm});
            skLineSegment(sketch, "E116.0.1.3", {"start": v(-386.2, -131.7) * mm, "end": v(-386.2, -119.7) * mm});
            skLineSegment(sketch, "E116.0.1.4", {"start": v(-406.2, -131.7) * mm, "end": v(-406.2, -119.7) * mm});
            skPoint(sketch, "E116.0.1.5", {"position": v(-406.2, -115.7) * mm});
            skPoint(sketch, "E116.0.1.6", {"position": v(-406.2, -135.7) * mm});
            skPoint(sketch, "E116.0.1.7", {"position": v(-396.2, -125.7) * mm});
            skPoint(sketch, "E116.0.1.8", {"position": v(-386.2, -135.7) * mm});
            skPoint(sketch, "E116.0.1.9", {"position": v(-396.2, -125.7) * mm});
            skArc(sketch, "E116.0.1.10", {"start": v(-390.2, -135.7) * mm, "mid": v(-387.37, -134.53) * mm, "end": v(-386.2, -131.7) * mm});
            skArc(sketch, "E116.0.1.11", {"start": v(-386.2, -119.7) * mm, "mid": v(-387.37, -116.88) * mm, "end": v(-390.2, -115.7) * mm});
            skArc(sketch, "E116.0.1.12", {"start": v(-402.2, -115.7) * mm, "mid": v(-405.03, -116.88) * mm, "end": v(-406.2, -119.7) * mm});
            skPoint(sketch, "E116.0.1.13", {"position": v(-396.2, -125.7) * mm});
            skArc(sketch, "E116.0.1.14", {"start": v(-406.2, -131.7) * mm, "mid": v(-405.03, -134.53) * mm, "end": v(-402.2, -135.7) * mm});
            skPoint(sketch, "E116.1.0.0", {"position": v(-305.2, -196.7) * mm});
            skLineSegment(sketch, "E116.1.0.1", {"start": v(-309.2, -216.7) * mm, "end": v(-321.2, -216.7) * mm});
            skLineSegment(sketch, "E116.1.0.2", {"start": v(-309.2, -196.7) * mm, "end": v(-321.2, -196.7) * mm});
            skLineSegment(sketch, "E116.1.0.3", {"start": v(-305.2, -212.7) * mm, "end": v(-305.2, -200.7) * mm});
            skLineSegment(sketch, "E116.1.0.4", {"start": v(-325.2, -212.7) * mm, "end": v(-325.2, -200.7) * mm});
            skPoint(sketch, "E116.1.0.5", {"position": v(-325.2, -196.7) * mm});
            skPoint(sketch, "E116.1.0.6", {"position": v(-325.2, -216.7) * mm});
            skPoint(sketch, "E116.1.0.7", {"position": v(-315.2, -206.7) * mm});
            skPoint(sketch, "E116.1.0.8", {"position": v(-305.2, -216.7) * mm});
            skPoint(sketch, "E116.1.0.9", {"position": v(-315.2, -206.7) * mm});
            skArc(sketch, "E116.1.0.10", {"start": v(-309.2, -216.7) * mm, "mid": v(-306.37, -215.53) * mm, "end": v(-305.2, -212.7) * mm});
            skArc(sketch, "E116.1.0.11", {"start": v(-305.2, -200.7) * mm, "mid": v(-306.37, -197.88) * mm, "end": v(-309.2, -196.7) * mm});
            skArc(sketch, "E116.1.0.12", {"start": v(-321.2, -196.7) * mm, "mid": v(-324.03, -197.88) * mm, "end": v(-325.2, -200.7) * mm});
            skPoint(sketch, "E116.1.0.13", {"position": v(-315.2, -206.7) * mm});
            skArc(sketch, "E116.1.0.14", {"start": v(-325.2, -212.7) * mm, "mid": v(-324.03, -215.53) * mm, "end": v(-321.2, -216.7) * mm});
            skPoint(sketch, "E116.1.1.0", {"position": v(-305.2, -115.7) * mm});
            skLineSegment(sketch, "E116.1.1.1", {"start": v(-309.2, -135.7) * mm, "end": v(-321.2, -135.7) * mm});
            skLineSegment(sketch, "E116.1.1.2", {"start": v(-309.2, -115.7) * mm, "end": v(-321.2, -115.7) * mm});
            skLineSegment(sketch, "E116.1.1.3", {"start": v(-305.2, -131.7) * mm, "end": v(-305.2, -119.7) * mm});
            skLineSegment(sketch, "E116.1.1.4", {"start": v(-325.2, -131.7) * mm, "end": v(-325.2, -119.7) * mm});
            skPoint(sketch, "E116.1.1.5", {"position": v(-325.2, -115.7) * mm});
            skPoint(sketch, "E116.1.1.6", {"position": v(-325.2, -135.7) * mm});
            skPoint(sketch, "E116.1.1.7", {"position": v(-315.2, -125.7) * mm});
            skPoint(sketch, "E116.1.1.8", {"position": v(-305.2, -135.7) * mm});
            skPoint(sketch, "E116.1.1.9", {"position": v(-315.2, -125.7) * mm});
            skArc(sketch, "E116.1.1.10", {"start": v(-309.2, -135.7) * mm, "mid": v(-306.37, -134.53) * mm, "end": v(-305.2, -131.7) * mm});
            skArc(sketch, "E116.1.1.11", {"start": v(-305.2, -119.7) * mm, "mid": v(-306.37, -116.88) * mm, "end": v(-309.2, -115.7) * mm});
            skArc(sketch, "E116.1.1.12", {"start": v(-321.2, -115.7) * mm, "mid": v(-324.03, -116.88) * mm, "end": v(-325.2, -119.7) * mm});
            skPoint(sketch, "E116.1.1.13", {"position": v(-315.2, -125.7) * mm});
            skArc(sketch, "E116.1.1.14", {"start": v(-325.2, -131.7) * mm, "mid": v(-324.03, -134.53) * mm, "end": v(-321.2, -135.7) * mm});
            skPoint(sketch, "E116.2.0.0", {"position": v(-224.2, -196.7) * mm});
            skLineSegment(sketch, "E116.2.0.1", {"start": v(-228.2, -216.7) * mm, "end": v(-240.2, -216.7) * mm});
            skLineSegment(sketch, "E116.2.0.2", {"start": v(-228.2, -196.7) * mm, "end": v(-240.2, -196.7) * mm});
            skLineSegment(sketch, "E116.2.0.3", {"start": v(-224.2, -212.7) * mm, "end": v(-224.2, -200.7) * mm});
            skLineSegment(sketch, "E116.2.0.4", {"start": v(-244.2, -212.7) * mm, "end": v(-244.2, -200.7) * mm});
            skPoint(sketch, "E116.2.0.5", {"position": v(-244.2, -196.7) * mm});
            skPoint(sketch, "E116.2.0.6", {"position": v(-244.2, -216.7) * mm});
            skPoint(sketch, "E116.2.0.7", {"position": v(-234.2, -206.7) * mm});
            skPoint(sketch, "E116.2.0.8", {"position": v(-224.2, -216.7) * mm});
            skPoint(sketch, "E116.2.0.9", {"position": v(-234.2, -206.7) * mm});
            skArc(sketch, "E116.2.0.10", {"start": v(-228.2, -216.7) * mm, "mid": v(-225.37, -215.53) * mm, "end": v(-224.2, -212.7) * mm});
            skArc(sketch, "E116.2.0.11", {"start": v(-224.2, -200.7) * mm, "mid": v(-225.37, -197.88) * mm, "end": v(-228.2, -196.7) * mm});
            skArc(sketch, "E116.2.0.12", {"start": v(-240.2, -196.7) * mm, "mid": v(-243.03, -197.88) * mm, "end": v(-244.2, -200.7) * mm});
            skPoint(sketch, "E116.2.0.13", {"position": v(-234.2, -206.7) * mm});
            skArc(sketch, "E116.2.0.14", {"start": v(-244.2, -212.7) * mm, "mid": v(-243.03, -215.53) * mm, "end": v(-240.2, -216.7) * mm});
            skPoint(sketch, "E116.2.1.0", {"position": v(-224.2, -115.7) * mm});
            skLineSegment(sketch, "E116.2.1.1", {"start": v(-228.2, -135.7) * mm, "end": v(-240.2, -135.7) * mm});
            skLineSegment(sketch, "E116.2.1.2", {"start": v(-228.2, -115.7) * mm, "end": v(-240.2, -115.7) * mm});
            skLineSegment(sketch, "E116.2.1.3", {"start": v(-224.2, -131.7) * mm, "end": v(-224.2, -119.7) * mm});
            skLineSegment(sketch, "E116.2.1.4", {"start": v(-244.2, -131.7) * mm, "end": v(-244.2, -119.7) * mm});
            skPoint(sketch, "E116.2.1.5", {"position": v(-244.2, -115.7) * mm});
            skPoint(sketch, "E116.2.1.6", {"position": v(-244.2, -135.7) * mm});
            skPoint(sketch, "E116.2.1.7", {"position": v(-234.2, -125.7) * mm});
            skPoint(sketch, "E116.2.1.8", {"position": v(-224.2, -135.7) * mm});
            skPoint(sketch, "E116.2.1.9", {"position": v(-234.2, -125.7) * mm});
            skArc(sketch, "E116.2.1.10", {"start": v(-228.2, -135.7) * mm, "mid": v(-225.37, -134.53) * mm, "end": v(-224.2, -131.7) * mm});
            skArc(sketch, "E116.2.1.11", {"start": v(-224.2, -119.7) * mm, "mid": v(-225.37, -116.88) * mm, "end": v(-228.2, -115.7) * mm});
            skArc(sketch, "E116.2.1.12", {"start": v(-240.2, -115.7) * mm, "mid": v(-243.03, -116.88) * mm, "end": v(-244.2, -119.7) * mm});
            skPoint(sketch, "E116.2.1.13", {"position": v(-234.2, -125.7) * mm});
            skArc(sketch, "E116.2.1.14", {"start": v(-244.2, -131.7) * mm, "mid": v(-243.03, -134.53) * mm, "end": v(-240.2, -135.7) * mm});
            skPoint(sketch, "E116.3.0.0", {"position": v(-143.2, -196.7) * mm});
            skLineSegment(sketch, "E116.3.0.1", {"start": v(-147.2, -216.7) * mm, "end": v(-159.2, -216.7) * mm});
            skLineSegment(sketch, "E116.3.0.2", {"start": v(-147.2, -196.7) * mm, "end": v(-159.2, -196.7) * mm});
            skLineSegment(sketch, "E116.3.0.3", {"start": v(-143.2, -212.7) * mm, "end": v(-143.2, -200.7) * mm});
            skLineSegment(sketch, "E116.3.0.4", {"start": v(-163.2, -212.7) * mm, "end": v(-163.2, -200.7) * mm});
            skPoint(sketch, "E116.3.0.5", {"position": v(-163.2, -196.7) * mm});
            skPoint(sketch, "E116.3.0.6", {"position": v(-163.2, -216.7) * mm});
            skPoint(sketch, "E116.3.0.7", {"position": v(-153.2, -206.7) * mm});
            skPoint(sketch, "E116.3.0.8", {"position": v(-143.2, -216.7) * mm});
            skPoint(sketch, "E116.3.0.9", {"position": v(-153.2, -206.7) * mm});
            skArc(sketch, "E116.3.0.10", {"start": v(-147.2, -216.7) * mm, "mid": v(-144.37, -215.53) * mm, "end": v(-143.2, -212.7) * mm});
            skArc(sketch, "E116.3.0.11", {"start": v(-143.2, -200.7) * mm, "mid": v(-144.37, -197.88) * mm, "end": v(-147.2, -196.7) * mm});
            skArc(sketch, "E116.3.0.12", {"start": v(-159.2, -196.7) * mm, "mid": v(-162.03, -197.88) * mm, "end": v(-163.2, -200.7) * mm});
            skPoint(sketch, "E116.3.0.13", {"position": v(-153.2, -206.7) * mm});
            skArc(sketch, "E116.3.0.14", {"start": v(-163.2, -212.7) * mm, "mid": v(-162.03, -215.53) * mm, "end": v(-159.2, -216.7) * mm});
            skPoint(sketch, "E116.3.1.0", {"position": v(-143.2, -115.7) * mm});
            skLineSegment(sketch, "E116.3.1.1", {"start": v(-147.2, -135.7) * mm, "end": v(-159.2, -135.7) * mm});
            skLineSegment(sketch, "E116.3.1.2", {"start": v(-147.2, -115.7) * mm, "end": v(-159.2, -115.7) * mm});
            skLineSegment(sketch, "E116.3.1.3", {"start": v(-143.2, -131.7) * mm, "end": v(-143.2, -119.7) * mm});
            skLineSegment(sketch, "E116.3.1.4", {"start": v(-163.2, -131.7) * mm, "end": v(-163.2, -119.7) * mm});
            skPoint(sketch, "E116.3.1.5", {"position": v(-163.2, -115.7) * mm});
            skPoint(sketch, "E116.3.1.6", {"position": v(-163.2, -135.7) * mm});
            skPoint(sketch, "E116.3.1.7", {"position": v(-153.2, -125.7) * mm});
            skPoint(sketch, "E116.3.1.8", {"position": v(-143.2, -135.7) * mm});
            skPoint(sketch, "E116.3.1.9", {"position": v(-153.2, -125.7) * mm});
            skArc(sketch, "E116.3.1.10", {"start": v(-147.2, -135.7) * mm, "mid": v(-144.37, -134.53) * mm, "end": v(-143.2, -131.7) * mm});
            skArc(sketch, "E116.3.1.11", {"start": v(-143.2, -119.7) * mm, "mid": v(-144.37, -116.88) * mm, "end": v(-147.2, -115.7) * mm});
            skArc(sketch, "E116.3.1.12", {"start": v(-159.2, -115.7) * mm, "mid": v(-162.03, -116.88) * mm, "end": v(-163.2, -119.7) * mm});
            skPoint(sketch, "E116.3.1.13", {"position": v(-153.2, -125.7) * mm});
            skArc(sketch, "E116.3.1.14", {"start": v(-163.2, -131.7) * mm, "mid": v(-162.03, -134.53) * mm, "end": v(-159.2, -135.7) * mm});
            skLineSegment(sketch, "E116.direction1", {"start": v(-406.2, -216.7) * mm, "end": v(-325.2, -216.7) * mm, "construction": true});
            skLineSegment(sketch, "E116.direction2", {"start": v(-406.2, -216.7) * mm, "end": v(-406.2, -135.7) * mm, "construction": true});
            skLineSegment(sketch, "E117.bottom", {"start": v(-430.7, -176.2) * mm, "end": v(-442.7, -176.2) * mm});
            skLineSegment(sketch, "E117.top", {"start": v(-430.7, -156.2) * mm, "end": v(-442.7, -156.2) * mm});
            skLineSegment(sketch, "E117.left", {"start": v(-426.7, -172.2) * mm, "end": v(-426.7, -160.2) * mm});
            skLineSegment(sketch, "E117.right", {"start": v(-446.7, -172.2) * mm, "end": v(-446.7, -160.2) * mm});
            skPoint(sketch, "E118.visualSharp", {"position": v(-426.7, -156.2) * mm});
            skArc(sketch, "E118.filletArc", {"start": v(-426.7, -160.2) * mm, "mid": v(-427.87, -157.38) * mm, "end": v(-430.7, -156.2) * mm});
            skPoint(sketch, "E119.visualSharp", {"position": v(-426.7, -176.2) * mm});
            skArc(sketch, "E119.filletArc", {"start": v(-430.7, -176.2) * mm, "mid": v(-427.87, -175.03) * mm, "end": v(-426.7, -172.2) * mm});
            skPoint(sketch, "E120.visualSharp", {"position": v(-446.7, -156.2) * mm});
            skArc(sketch, "E120.filletArc", {"start": v(-442.7, -156.2) * mm, "mid": v(-445.53, -157.38) * mm, "end": v(-446.7, -160.2) * mm});
            skPoint(sketch, "E121.visualSharp", {"position": v(-446.7, -176.2) * mm});
            skArc(sketch, "E121.filletArc", {"start": v(-446.7, -172.2) * mm, "mid": v(-445.53, -175.03) * mm, "end": v(-442.7, -176.2) * mm});
            skPoint(sketch, "E122.1.0.0", {"position": v(-365.7, -156.2) * mm});
            skLineSegment(sketch, "E122.1.0.1", {"start": v(-365.7, -172.2) * mm, "end": v(-365.7, -160.2) * mm});
            skPoint(sketch, "E122.1.0.2", {"position": v(-345.7, -176.2) * mm});
            skLineSegment(sketch, "E122.1.0.3", {"start": v(-349.7, -176.2) * mm, "end": v(-361.7, -176.2) * mm});
            skPoint(sketch, "E122.1.0.4", {"position": v(-365.7, -176.2) * mm});
            skLineSegment(sketch, "E122.1.0.5", {"start": v(-345.7, -172.2) * mm, "end": v(-345.7, -160.2) * mm});
            skPoint(sketch, "E122.1.0.6", {"position": v(-345.7, -156.2) * mm});
            skLineSegment(sketch, "E122.1.0.7", {"start": v(-349.7, -156.2) * mm, "end": v(-361.7, -156.2) * mm});
            skPoint(sketch, "E122.1.0.8", {"position": v(-355.7, -166.2) * mm});
            skPoint(sketch, "E122.1.0.9", {"position": v(-355.7, -166.2) * mm});
            skArc(sketch, "E122.1.0.10", {"start": v(-361.7, -156.2) * mm, "mid": v(-364.53, -157.38) * mm, "end": v(-365.7, -160.2) * mm});
            skArc(sketch, "E122.1.0.11", {"start": v(-349.7, -176.2) * mm, "mid": v(-346.87, -175.03) * mm, "end": v(-345.7, -172.2) * mm});
            skArc(sketch, "E122.1.0.12", {"start": v(-345.7, -160.2) * mm, "mid": v(-346.87, -157.38) * mm, "end": v(-349.7, -156.2) * mm});
            skArc(sketch, "E122.1.0.13", {"start": v(-365.7, -172.2) * mm, "mid": v(-364.53, -175.03) * mm, "end": v(-361.7, -176.2) * mm});
            skPoint(sketch, "E122.2.0.0", {"position": v(-284.7, -156.2) * mm});
            skLineSegment(sketch, "E122.2.0.1", {"start": v(-284.7, -172.2) * mm, "end": v(-284.7, -160.2) * mm});
            skPoint(sketch, "E122.2.0.2", {"position": v(-264.7, -176.2) * mm});
            skLineSegment(sketch, "E122.2.0.3", {"start": v(-268.7, -176.2) * mm, "end": v(-280.7, -176.2) * mm});
            skPoint(sketch, "E122.2.0.4", {"position": v(-284.7, -176.2) * mm});
            skLineSegment(sketch, "E122.2.0.5", {"start": v(-264.7, -172.2) * mm, "end": v(-264.7, -160.2) * mm});
            skPoint(sketch, "E122.2.0.6", {"position": v(-264.7, -156.2) * mm});
            skLineSegment(sketch, "E122.2.0.7", {"start": v(-268.7, -156.2) * mm, "end": v(-280.7, -156.2) * mm});
            skPoint(sketch, "E122.2.0.8", {"position": v(-274.7, -166.2) * mm});
            skPoint(sketch, "E122.2.0.9", {"position": v(-274.7, -166.2) * mm});
            skArc(sketch, "E122.2.0.10", {"start": v(-280.7, -156.2) * mm, "mid": v(-283.53, -157.38) * mm, "end": v(-284.7, -160.2) * mm});
            skArc(sketch, "E122.2.0.11", {"start": v(-268.7, -176.2) * mm, "mid": v(-265.87, -175.03) * mm, "end": v(-264.7, -172.2) * mm});
            skArc(sketch, "E122.2.0.12", {"start": v(-264.7, -160.2) * mm, "mid": v(-265.87, -157.38) * mm, "end": v(-268.7, -156.2) * mm});
            skArc(sketch, "E122.2.0.13", {"start": v(-284.7, -172.2) * mm, "mid": v(-283.53, -175.03) * mm, "end": v(-280.7, -176.2) * mm});
            skPoint(sketch, "E122.3.0.0", {"position": v(-203.7, -156.2) * mm});
            skLineSegment(sketch, "E122.3.0.1", {"start": v(-203.7, -172.2) * mm, "end": v(-203.7, -160.2) * mm});
            skPoint(sketch, "E122.3.0.2", {"position": v(-183.7, -176.2) * mm});
            skLineSegment(sketch, "E122.3.0.3", {"start": v(-187.7, -176.2) * mm, "end": v(-199.7, -176.2) * mm});
            skPoint(sketch, "E122.3.0.4", {"position": v(-203.7, -176.2) * mm});
            skLineSegment(sketch, "E122.3.0.5", {"start": v(-183.7, -172.2) * mm, "end": v(-183.7, -160.2) * mm});
            skPoint(sketch, "E122.3.0.6", {"position": v(-183.7, -156.2) * mm});
            skLineSegment(sketch, "E122.3.0.7", {"start": v(-187.7, -156.2) * mm, "end": v(-199.7, -156.2) * mm});
            skPoint(sketch, "E122.3.0.8", {"position": v(-193.7, -166.2) * mm});
            skPoint(sketch, "E122.3.0.9", {"position": v(-193.7, -166.2) * mm});
            skArc(sketch, "E122.3.0.10", {"start": v(-199.7, -156.2) * mm, "mid": v(-202.53, -157.38) * mm, "end": v(-203.7, -160.2) * mm});
            skArc(sketch, "E122.3.0.11", {"start": v(-187.7, -176.2) * mm, "mid": v(-184.87, -175.03) * mm, "end": v(-183.7, -172.2) * mm});
            skArc(sketch, "E122.3.0.12", {"start": v(-183.7, -160.2) * mm, "mid": v(-184.87, -157.38) * mm, "end": v(-187.7, -156.2) * mm});
            skArc(sketch, "E122.3.0.13", {"start": v(-203.7, -172.2) * mm, "mid": v(-202.53, -175.03) * mm, "end": v(-199.7, -176.2) * mm});
            skPoint(sketch, "E122.4.0.0", {"position": v(-122.7, -156.2) * mm});
            skLineSegment(sketch, "E122.4.0.1", {"start": v(-122.7, -172.2) * mm, "end": v(-122.7, -160.2) * mm});
            skPoint(sketch, "E122.4.0.2", {"position": v(-102.7, -176.2) * mm});
            skLineSegment(sketch, "E122.4.0.3", {"start": v(-106.7, -176.2) * mm, "end": v(-118.7, -176.2) * mm});
            skPoint(sketch, "E122.4.0.4", {"position": v(-122.7, -176.2) * mm});
            skLineSegment(sketch, "E122.4.0.5", {"start": v(-102.7, -172.2) * mm, "end": v(-102.7, -160.2) * mm});
            skPoint(sketch, "E122.4.0.6", {"position": v(-102.7, -156.2) * mm});
            skLineSegment(sketch, "E122.4.0.7", {"start": v(-106.7, -156.2) * mm, "end": v(-118.7, -156.2) * mm});
            skPoint(sketch, "E122.4.0.8", {"position": v(-112.7, -166.2) * mm});
            skPoint(sketch, "E122.4.0.9", {"position": v(-112.7, -166.2) * mm});
            skArc(sketch, "E122.4.0.10", {"start": v(-118.7, -156.2) * mm, "mid": v(-121.53, -157.38) * mm, "end": v(-122.7, -160.2) * mm});
            skArc(sketch, "E122.4.0.11", {"start": v(-106.7, -176.2) * mm, "mid": v(-103.87, -175.03) * mm, "end": v(-102.7, -172.2) * mm});
            skArc(sketch, "E122.4.0.12", {"start": v(-102.7, -160.2) * mm, "mid": v(-103.87, -157.38) * mm, "end": v(-106.7, -156.2) * mm});
            skArc(sketch, "E122.4.0.13", {"start": v(-122.7, -172.2) * mm, "mid": v(-121.53, -175.03) * mm, "end": v(-118.7, -176.2) * mm});
            skLineSegment(sketch, "E122.direction1", {"start": v(-446.7, -176.2) * mm, "end": v(-365.7, -176.2) * mm, "construction": true});
            skLineSegment(sketch, "E123.bottom", {"start": v(-562.98, 16.43) * mm, "end": v(-572.98, 16.43) * mm});
            skLineSegment(sketch, "E123.top", {"start": v(-562.98, 31.43) * mm, "end": v(-572.98, 31.43) * mm});
            skLineSegment(sketch, "E123.left", {"start": v(-562.98, 16.43) * mm, "end": v(-562.98, 31.43) * mm});
            skLineSegment(sketch, "E123.right", {"start": v(-572.98, 16.43) * mm, "end": v(-572.98, 31.43) * mm});
            skPoint(sketch, "E123.middle", {"position": v(-567.98, 23.93) * mm});
            skSolve(sketch);
        }
        {
            var Q0;
            Q0=makeQuery(id+"F0.imprint","IMPRINT",FACE,{"disambiguationData":[TD([[makeQuery(id+"F0.imprint","IMPRINT",EDGE,{"derivedFrom":sQuery(id+"F0.wireOp",EDGE,"Fney506r-Qcku-IDu7-psrx-d7xNBIuqF4b9.bottom")}),1.0]])]});
            var Q1;
            Q1=makeQuery(id+"F0.imprint","IMPRINT",FACE,{"disambiguationData":[TD([[makeQuery(id+"F0.imprint","IMPRINT",EDGE,{"derivedFrom":sQuery(id+"F0.wireOp",EDGE,"5JMTg0qh-CgCK-IdQi-9wzY-HiJAbUdymWVC.bottom")}),-1.0]])]});
            var Q2;
            Q2=makeQuery(id+"F0.imprint","IMPRINT",FACE,{"disambiguationData":[TD([[makeQuery(id+"F0.imprint","IMPRINT",EDGE,{"derivedFrom":sQuery(id+"F0.wireOp",EDGE,"E1.bottom")}),1.0]])]});
            var Q3;
            Q3=makeQuery(id+"F0.imprint","IMPRINT",FACE,{"disambiguationData":[TD([[makeQuery(id+"F0.imprint","IMPRINT",EDGE,{"derivedFrom":sQuery(id+"F0.wireOp",EDGE,"E2.bottom")}),-1.0]])]});
            var Q4;
            {var subQ15=sQuery(id+"F0.wireOp",EDGE,"ZBVLCXsl-KTdY-y0b7-p4dx-gQjgQsivWRCQ.bottom");Q4=makeQuery(id+"F0.imprint","IMPRINT",FACE,{"disambiguationData":[TD([[makeQuery(id+"F0.imprint","IMPRINT",EDGE,{"derivedFrom":subQ15}),-1.0]])]});}
            var Q5;
            Q5=makeQuery(id+"F0.imprint","IMPRINT",FACE,{"disambiguationData":[TD([[makeQuery(id+"F0.imprint","IMPRINT",EDGE,{"derivedFrom":sQuery(id+"F0.wireOp",EDGE,"E0.top")}),1.0]])]});
            var Q6;
            Q6=makeQuery(id+"F0.imprint","IMPRINT",FACE,{"disambiguationData":[TD([[makeQuery(id+"F0.imprint","IMPRINT",EDGE,{"derivedFrom":sQuery(id+"F0.wireOp",EDGE,"f4d3a21f-fe50-4398-bfb2-a687dcf9783f.bottom")}),-1.0]])]});
            var Q7;
            Q7=makeQuery(id+"F0.imprint","IMPRINT",FACE,{"disambiguationData":[TD([[makeQuery(id+"F0.imprint","IMPRINT",EDGE,{"derivedFrom":sQuery(id+"F0.wireOp",EDGE,"062292ec-e78f-4c67-a23f-dd19eec59be2.bottom")}),-1.0]])]});
            var Q8;
            Q8=makeQuery(id+"F0.imprint","IMPRINT",FACE,{"disambiguationData":[TD([[makeQuery(id+"F0.imprint","IMPRINT",EDGE,{"derivedFrom":sQuery(id+"F0.wireOp",EDGE,"d9409766-82f2-4483-9d12-0a5b3a1678c7.bottom")}),1.0]])]});
            var Q9;
            Q9=makeQuery(id+"F0.imprint","IMPRINT",FACE,{"disambiguationData":[TD([[makeQuery(id+"F0.imprint","IMPRINT",EDGE,{"derivedFrom":sQuery(id+"F0.wireOp",EDGE,"21800fcb-d17b-4c61-97d0-9fb2fdc64302.bottom")}),-1.0]])]});
            var Q10;
            Q10=makeQuery(id+"F0.imprint","IMPRINT",FACE,{"disambiguationData":[TD([[makeQuery(id+"F0.imprint","IMPRINT",EDGE,{"derivedFrom":sQuery(id+"F0.wireOp",EDGE,"4ac69527-0d6d-4a96-af52-274d03c91bb4.bottom")}),1.0]])]});
            var Q11;
            Q11=makeQuery(id+"F0.imprint","IMPRINT",FACE,{"disambiguationData":[TD([[makeQuery(id+"F0.imprint","IMPRINT",EDGE,{"derivedFrom":sQuery(id+"F0.wireOp",EDGE,"c15bb839-e76e-4ff4-a0e4-7561f68a4473.bottom")}),-1.0]])]});
            var Q12;
            Q12=makeQuery(id+"F0.imprint","IMPRINT",FACE,{"disambiguationData":[TD([[makeQuery(id+"F0.imprint","IMPRINT",EDGE,{"derivedFrom":sQuery(id+"F0.wireOp",EDGE,"12cb7520-e1c7-4f3f-86fd-d2fb80b1a012.bottom")}),1.0]])]});
            var Q13;
            Q13=makeQuery(id+"F0.imprint","IMPRINT",FACE,{"disambiguationData":[TD([[makeQuery(id+"F0.imprint","IMPRINT",EDGE,{"derivedFrom":sQuery(id+"F0.wireOp",EDGE,"f3b0d050-efba-4abe-9bf6-5166f67fa48c.bottom")}),-1.0]])]});
            var Q14;
            Q14=makeQuery(id+"F0.imprint","IMPRINT",FACE,{"disambiguationData":[TD([[makeQuery(id+"F0.imprint","IMPRINT",EDGE,{"derivedFrom":sQuery(id+"F0.wireOp",EDGE,"b5fed350-8060-4531-918e-057eb5c30298.bottom")}),-1.0]])]});
            var Q15;
            Q15=makeQuery(id+"F0.imprint","IMPRINT",FACE,{"disambiguationData":[TD([[makeQuery(id+"F0.imprint","IMPRINT",EDGE,{"derivedFrom":sQuery(id+"F0.wireOp",EDGE,"E28.bottom")}),-1.0]])]});
            var Q16;
            Q16=makeQuery(id+"F0.imprint","IMPRINT",FACE,{"disambiguationData":[TD([[makeQuery(id+"F0.imprint","IMPRINT",EDGE,{"derivedFrom":sQuery(id+"F0.wireOp",EDGE,"E29.bottom")}),1.0]])]});
            var Q17;
            Q17=makeQuery(id+"F0.imprint","IMPRINT",FACE,{"disambiguationData":[TD([[makeQuery(id+"F0.imprint","IMPRINT",EDGE,{"derivedFrom":sQuery(id+"F0.wireOp",EDGE,"E30.bottom")}),-1.0]])]});
            var Q18;
            Q18=makeQuery(id+"F0.imprint","IMPRINT",FACE,{"disambiguationData":[TD([[makeQuery(id+"F0.imprint","IMPRINT",EDGE,{"derivedFrom":sQuery(id+"F0.wireOp",EDGE,"E75.bottom")}),-1.0]])]});
            var Q19;
            Q19=makeQuery(id+"F0.imprint","IMPRINT",FACE,{"disambiguationData":[TD([[makeQuery(id+"F0.imprint","IMPRINT",EDGE,{"derivedFrom":sQuery(id+"F0.wireOp",EDGE,"E73.bottom")}),-1.0]])]});
            var Q20;
            Q20=makeQuery(id+"F0.imprint","IMPRINT",FACE,{"disambiguationData":[TD([[makeQuery(id+"F0.imprint","IMPRINT",EDGE,{"derivedFrom":sQuery(id+"F0.wireOp",EDGE,"E74.bottom")}),1.0]])]});
            extrude(context, id + "F1", {"entities" : qUnion([Q0, Q1, Q2, Q3, Q4, Q5, Q6, Q7, Q8, Q9, Q10, Q11, Q12, Q13, Q14, Q15, Q16, Q17, Q18, Q19, Q20]), "depth" : 3 * mm, "offsetDistance" : 25 * mm});
        }
        {
            var Q0;
            Q0 = qSketchRegion(id + "F0", true);
            extrude(context, id + "F2", {"entities" : qUnion([Q0]), "depth" : 3 * mm, "offsetDistance" : 25 * mm});
        }
        {
            var Q0;
            Q0=makeQuery(id+"F2.opExtrude","CAP_FACE",FACE,{"disambiguationData":[OSD([sQuery(id+"F0.wireOp",EDGE,"E123.bottom"),sQuery(id+"F0.wireOp",EDGE,"E123.top"),sQuery(id+"F0.wireOp",EDGE,"E123.left"),sQuery(id+"F0.wireOp",EDGE,"E123.right")])],"isStart":false});
            extrude(context, id + "F3", {"entities" : qUnion([Q0]), "operationType" : NewBodyOperationType.ADD, "depth" : 4.5 * mm, "offsetDistance" : 25 * mm});
        }
    });
